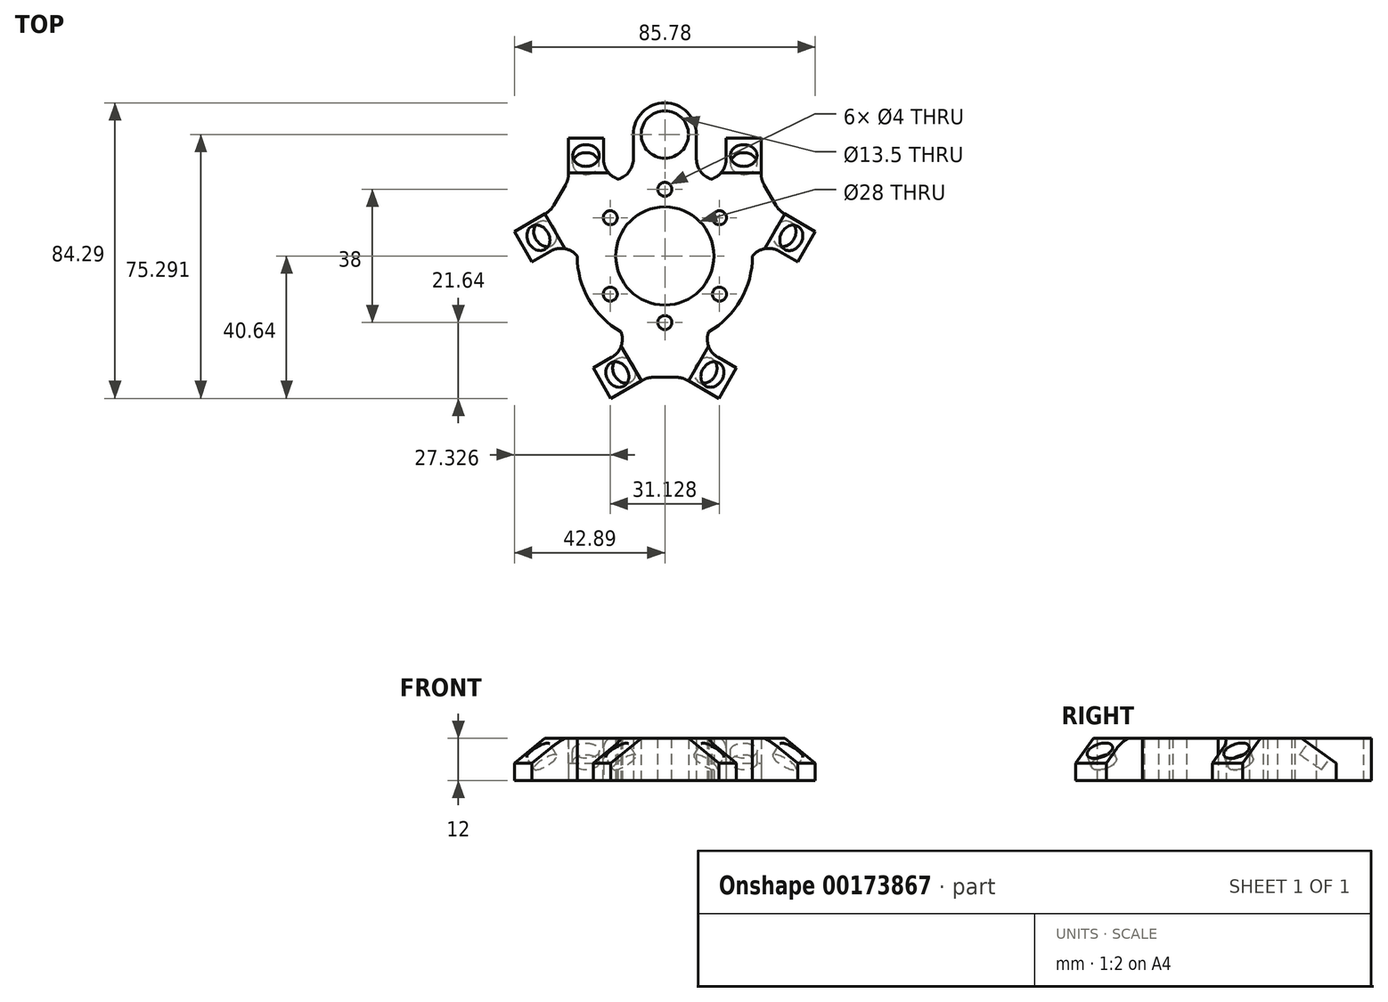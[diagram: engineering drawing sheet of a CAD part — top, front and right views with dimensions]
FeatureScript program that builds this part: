
annotation { "Feature Type Name" : "Feature", "Feature Type Description" : "" }
export const myFeature = defineFeature(function(context is Context, id is Id, definition is map)
    precondition{}
    {
        {
            var Q0;
            Q0=qCreatedBy(makeId("Top.planeOp"),FACE);
            var sketch = newSketch(context, id + "F0", { "sketchPlane" : qUnion([Q0])});
            skCircle(sketch, "E0.cCircle", {"center": v(0, 0) * mm, "radius": 21.65 * mm, "construction": true});
            skLineSegment(sketch, "E0.0", {"start": v(-37.5, 21.65) * mm, "end": v(37.5, 21.65) * mm});
            skLineSegment(sketch, "E0.1", {"start": v(37.5, 21.65) * mm, "end": v(0, -43.3) * mm});
            skLineSegment(sketch, "E0.2", {"start": v(0, -43.3) * mm, "end": v(-37.5, 21.65) * mm});
            skPoint(sketch, "E0.0.midPoint", {"position": v(0, 21.65) * mm});
            skLineSegment(sketch, "E1", {"start": v(-5, -34.64) * mm, "end": v(5, -34.64) * mm});
            skLineSegment(sketch, "E2", {"start": v(27.5, 21.65) * mm, "end": v(32.5, 13) * mm});
            skLineSegment(sketch, "E3", {"start": v(-17.5, 33.65) * mm, "end": v(-17.5, 21.65) * mm});
            skLineSegment(sketch, "E4", {"start": v(17.5, 21.65) * mm, "end": v(17.5, 33.65) * mm});
            skLineSegment(sketch, "E5", {"start": v(27.5, 33.65) * mm, "end": v(27.5, 21.65) * mm});
            skLineSegment(sketch, "E6", {"start": v(-27.5, 21.65) * mm, "end": v(-27.5, 33.65) * mm});
            skLineSegment(sketch, "E7.MirrorCS", {"start": v(32.5, 13) * mm, "end": v(42.9, 7) * mm});
            skLineSegment(sketch, "E8.MirrorCS", {"start": v(37.9, -1.67) * mm, "end": v(27.5, 4.33) * mm});
            skLineSegment(sketch, "E9.MirrorCS", {"start": v(10, -25.98) * mm, "end": v(20.4, -31.98) * mm});
            skLineSegment(sketch, "E10.MirrorCS", {"start": v(15.4, -40.64) * mm, "end": v(5, -34.64) * mm});
            skLineSegment(sketch, "E11", {"start": v(-42.9, 7) * mm, "end": v(-32.5, 13) * mm});
            skLineSegment(sketch, "E12", {"start": v(-37.9, -1.67) * mm, "end": v(-27.5, 4.33) * mm});
            skLineSegment(sketch, "E13", {"start": v(-20.4, -31.98) * mm, "end": v(-10, -25.98) * mm});
            skLineSegment(sketch, "E14", {"start": v(-15.4, -40.64) * mm, "end": v(-5, -34.64) * mm});
            skCircle(sketch, "E15", {"center": v(0, 0) * mm, "radius": 14 * mm});
            skLineSegment(sketch, "E16", {"start": v(0, 21.65) * mm, "end": v(0, 34.65) * mm});
            skCircle(sketch, "E17", {"center": v(0, 34.65) * mm, "radius": 6.75 * mm});
            skArc(sketch, "E18", {"start": v(9, 34.65) * mm, "mid": v(0, 43.65) * mm, "end": v(-9, 34.65) * mm});
            skLineSegment(sketch, "E19", {"start": v(-9, 34.65) * mm, "end": v(-9, 21.65) * mm});
            skLineSegment(sketch, "E20", {"start": v(9, 34.65) * mm, "end": v(9, 21.65) * mm});
            skLineSegment(sketch, "E21", {"start": v(-32.5, 13) * mm, "end": v(-27.5, 21.65) * mm});
            skArc(sketch, "E22", {"start": v(-25, 0) * mm, "mid": v(-21.65, -12.5) * mm, "end": v(-12.5, -21.65) * mm});
            skArc(sketch, "E23.trimOffspring", {"start": v(12.5, -21.65) * mm, "mid": v(21.65, -12.5) * mm, "end": v(25, 0) * mm});
            skLineSegment(sketch, "E24", {"start": v(-37.9, -1.67) * mm, "end": v(-42.9, 7) * mm});
            skLineSegment(sketch, "E25", {"start": v(-27.5, 33.65) * mm, "end": v(-17.5, 33.65) * mm});
            skLineSegment(sketch, "E26", {"start": v(17.5, 33.65) * mm, "end": v(27.5, 33.65) * mm});
            skLineSegment(sketch, "E27", {"start": v(42.9, 7) * mm, "end": v(37.9, -1.67) * mm});
            skLineSegment(sketch, "E28", {"start": v(20.4, -31.98) * mm, "end": v(15.4, -40.64) * mm});
            skLineSegment(sketch, "E29", {"start": v(-15.4, -40.64) * mm, "end": v(-20.4, -31.98) * mm});
            skSolve(sketch);
        }
        {
            var Q0;
            {var subQ0=sQuery(id+"F0.wireOp",EDGE,"E3");Q0=makeQuery(id+"F0.imprint","IMPRINT",FACE,{"disambiguationData":[TD([[makeQuery(id+"F0.imprint","IMPRINT",EDGE,{"derivedFrom":subQ0}),-1.0]])]});}
            var Q1;
            Q1=makeQuery(id+"F0.imprint","IMPRINT",FACE,{"disambiguationData":[TD([[makeQuery(id+"F0.imprint","IMPRINT",EDGE,{"derivedFrom":sQuery(id+"F0.wireOp",EDGE,"E17")}),-1.0]])]});
            var Q2;
            {var subQ2=sQuery(id+"F0.wireOp",EDGE,"E4");Q2=makeQuery(id+"F0.imprint","IMPRINT",FACE,{"disambiguationData":[TD([[makeQuery(id+"F0.imprint","IMPRINT",EDGE,{"derivedFrom":subQ2}),-1.0]])]});}
            var Q3;
            {var subQ19=sQuery(id+"F0.wireOp",EDGE,"E1");Q3=makeQuery(id+"F0.imprint","IMPRINT",FACE,{"disambiguationData":[TD([[makeQuery(id+"F0.imprint","IMPRINT",EDGE,{"derivedFrom":subQ19}),1.0]])]});}
            var Q4;
            {var subQ0=sQuery(id+"F0.wireOp",EDGE,"E7.MirrorCS");Q4=makeQuery(id+"F0.imprint","IMPRINT",FACE,{"disambiguationData":[TD([[makeQuery(id+"F0.imprint","IMPRINT",EDGE,{"derivedFrom":subQ0}),-1.0]])]});}
            var Q5;
            {var subQ2=sQuery(id+"F0.wireOp",EDGE,"E9.MirrorCS");Q5=makeQuery(id+"F0.imprint","IMPRINT",FACE,{"disambiguationData":[TD([[makeQuery(id+"F0.imprint","IMPRINT",EDGE,{"derivedFrom":subQ2}),-1.0]])]});}
            var Q6;
            {var subQ0=sQuery(id+"F0.wireOp",EDGE,"E11");Q6=makeQuery(id+"F0.imprint","IMPRINT",FACE,{"disambiguationData":[TD([[makeQuery(id+"F0.imprint","IMPRINT",EDGE,{"derivedFrom":subQ0}),-1.0]])]});}
            var Q7;
            {var subQ0=sQuery(id+"F0.wireOp",EDGE,"E22");Q7=makeQuery(id+"F0.imprint","IMPRINT",FACE,{"disambiguationData":[TD([[makeQuery(id+"F0.imprint","IMPRINT",EDGE,{"derivedFrom":subQ0}),1.0]])]});}
            var Q8;
            {var subQ0=sQuery(id+"F0.wireOp",EDGE,"E23.trimOffspring");Q8=makeQuery(id+"F0.imprint","IMPRINT",FACE,{"disambiguationData":[TD([[makeQuery(id+"F0.imprint","IMPRINT",EDGE,{"derivedFrom":subQ0}),1.0]])]});}
            var Q9;
            {var subQ2=sQuery(id+"F0.wireOp",EDGE,"E13");Q9=makeQuery(id+"F0.imprint","IMPRINT",FACE,{"disambiguationData":[TD([[makeQuery(id+"F0.imprint","IMPRINT",EDGE,{"derivedFrom":subQ2}),-1.0]])]});}
            extrude(context, id + "F1", {"entities" : qUnion([Q0, Q1, Q2, Q3, Q4, Q5, Q6, Q7, Q8, Q9]), "depth" : 12 * mm});
        }
        {
            var Q0;
            Q0=makeQuery(id+"F1.opExtrude","CAP_EDGE",EDGE,{"disambiguationData":[OSD([sQuery(id+"F0.wireOp",EDGE,"E29")])],"isStart":false});
            var Q1;
            Q1=makeQuery(id+"F1.opExtrude","CAP_EDGE",EDGE,{"disambiguationData":[OSD([sQuery(id+"F0.wireOp",EDGE,"E24")])],"isStart":false});
            var Q2;
            Q2=makeQuery(id+"F1.opExtrude","CAP_EDGE",EDGE,{"disambiguationData":[OSD([sQuery(id+"F0.wireOp",EDGE,"E25")])],"isStart":false});
            var Q3;
            Q3=makeQuery(id+"F1.opExtrude","CAP_EDGE",EDGE,{"disambiguationData":[OSD([sQuery(id+"F0.wireOp",EDGE,"E26")])],"isStart":false});
            var Q4;
            Q4=makeQuery(id+"F1.opExtrude","CAP_EDGE",EDGE,{"disambiguationData":[OSD([sQuery(id+"F0.wireOp",EDGE,"E27")])],"isStart":false});
            var Q5;
            Q5=makeQuery(id+"F1.opExtrude","CAP_EDGE",EDGE,{"disambiguationData":[OSD([sQuery(id+"F0.wireOp",EDGE,"E28")])],"isStart":false});
            chamfer(context, id + "F2", {"entities" : qUnion([Q0, Q1, Q2, Q3, Q4, Q5]), "chamferType" : ChamferType.TWO_OFFSETS, "width1" : 7 * mm, "oppositeDirection" : false, "width2" : 10 * mm, "tangentPropagation" : true});
        }
        {
            var Q0;
            Q0=makeQuery(id+"F2.opChamfer","BLEND_FACE",FACE,{"disambiguationData":[OSD([sQuery(id+"F0.wireOp",EDGE,"E24")])]});
            var sketch = newSketch(context, id + "F3", { "sketchPlane" : qUnion([Q0])});
            skLineSegment(sketch, "E30", {"start": v(-31.04, 11.77) * mm, "end": v(-27.27, 6.41) * mm, "construction": true});
            skLineSegment(sketch, "E31", {"start": v(-33.15, 4.16) * mm, "end": v(-26.05, 9.16) * mm, "construction": true});
            skCircle(sketch, "E32", {"center": v(-28.16, 7.68) * mm, "radius": 3.8 * mm});
            skCircle(sketch, "E33", {"center": v(-2.24, -29.1) * mm, "radius": 3.8 * mm});
            skLineSegment(sketch, "E34", {"start": v(-28.16, 7.68) * mm, "end": v(-2.24, -29.1) * mm, "construction": true});
            skSolve(sketch);
        }
        {
            var Q0;
            Q0=makeQuery(id+"F3.imprint","IMPRINT",FACE,{"disambiguationData":[TD([[makeQuery(id+"F3.imprint","IMPRINT",EDGE,{"derivedFrom":sQuery(id+"F3.wireOp",EDGE,"E32")}),1.0]])]});
            var Q1;
            Q1=makeQuery(id+"F3.imprint","IMPRINT",FACE,{"disambiguationData":[TD([[makeQuery(id+"F3.imprint","IMPRINT",EDGE,{"derivedFrom":sQuery(id+"F3.wireOp",EDGE,"E33")}),1.0]])]});
            extrude(context, id + "F4", {"entities" : qUnion([Q0, Q1]), "operationType" : NewBodyOperationType.REMOVE, "oppositeDirection" : true, "depth" : 4 * mm});
        }
        {
            var Q0;
            Q0=makeQuery(id+"F2.opChamfer","BLEND_FACE",FACE,{"disambiguationData":[OSD([sQuery(id+"F0.wireOp",EDGE,"E26")])]});
            var sketch = newSketch(context, id + "F5", { "sketchPlane" : qUnion([Q0])});
            skLineSegment(sketch, "E35", {"start": v(27.5, 18.6) * mm, "end": v(22.5, 18.6) * mm});
            skLineSegment(sketch, "E36", {"start": v(22.5, 18.6) * mm, "end": v(-22.5, 18.6) * mm});
            skCircle(sketch, "E37", {"center": v(22.5, 18.6) * mm, "radius": 3.8 * mm});
            skCircle(sketch, "E38", {"center": v(-22.5, 18.6) * mm, "radius": 3.8 * mm});
            skSolve(sketch);
        }
        {
            var Q0;
            {var subQ0=sQuery(id+"F5.wireOp",EDGE,"E36");var subQ1=sQuery(id+"F5.wireOp",EDGE,"E35");var subQ2=makeQuery(id+"F5.imprint","INTERSECT",VERTEX,{"derivedFrom":[subQ1,subQ0]});Q0=makeQuery(id+"F5.imprint","IMPRINT",FACE,{"disambiguationData":[TD([[makeQuery(id+"F5.imprint","IMPRINT",EDGE,{"disambiguationData":[TD([[subQ2,1.0]])],"derivedFrom":subQ1}),1.0]])]});}
            var Q1;
            {var subQ0=sQuery(id+"F5.wireOp",EDGE,"E36");var subQ1=sQuery(id+"F5.wireOp",EDGE,"E35");var subQ2=makeQuery(id+"F5.imprint","INTERSECT",VERTEX,{"derivedFrom":[subQ1,subQ0]});Q1=makeQuery(id+"F5.imprint","IMPRINT",FACE,{"disambiguationData":[TD([[makeQuery(id+"F5.imprint","IMPRINT",EDGE,{"disambiguationData":[TD([[subQ2,1.0]])],"derivedFrom":subQ1}),-1.0]])]});}
            var Q2;
            Q2=makeQuery(id+"F5.imprint","IMPRINT",FACE,{"disambiguationData":[TD([[makeQuery(id+"F5.imprint","IMPRINT",EDGE,{"derivedFrom":sQuery(id+"F5.wireOp",EDGE,"E38")}),1.0]])]});
            extrude(context, id + "F6", {"entities" : qUnion([Q0, Q1, Q2]), "operationType" : NewBodyOperationType.REMOVE, "oppositeDirection" : true, "depth" : 4 * mm});
        }
        {
            var Q0;
            Q0=makeQuery(id+"F2.opChamfer","BLEND_FACE",FACE,{"disambiguationData":[OSD([sQuery(id+"F0.wireOp",EDGE,"E28")])]});
            var sketch = newSketch(context, id + "F7", { "sketchPlane" : qUnion([Q0])});
            skLineSegment(sketch, "E39", {"start": v(-0.64, -33.2) * mm, "end": v(2.24, -29.1) * mm});
            skLineSegment(sketch, "E40", {"start": v(2.24, -29.1) * mm, "end": v(28.16, 7.68) * mm});
            skCircle(sketch, "E41", {"center": v(2.24, -29.1) * mm, "radius": 3.8 * mm});
            skCircle(sketch, "E42", {"center": v(28.16, 7.68) * mm, "radius": 3.8 * mm});
            skSolve(sketch);
        }
        {
            var Q0;
            {var subQ0=sQuery(id+"F7.wireOp",EDGE,"E40");var subQ1=sQuery(id+"F7.wireOp",EDGE,"E39");var subQ2=makeQuery(id+"F7.imprint","INTERSECT",VERTEX,{"derivedFrom":[subQ1,subQ0]});Q0=makeQuery(id+"F7.imprint","IMPRINT",FACE,{"disambiguationData":[TD([[makeQuery(id+"F7.imprint","IMPRINT",EDGE,{"disambiguationData":[TD([[subQ2,1.0]])],"derivedFrom":subQ1}),-1.0]])]});}
            var Q1;
            {var subQ0=sQuery(id+"F7.wireOp",EDGE,"E40");var subQ1=sQuery(id+"F7.wireOp",EDGE,"E39");var subQ2=makeQuery(id+"F7.imprint","INTERSECT",VERTEX,{"derivedFrom":[subQ1,subQ0]});Q1=makeQuery(id+"F7.imprint","IMPRINT",FACE,{"disambiguationData":[TD([[makeQuery(id+"F7.imprint","IMPRINT",EDGE,{"disambiguationData":[TD([[subQ2,1.0]])],"derivedFrom":subQ1}),1.0]])]});}
            var Q2;
            Q2=makeQuery(id+"F7.imprint","IMPRINT",FACE,{"disambiguationData":[TD([[makeQuery(id+"F7.imprint","IMPRINT",EDGE,{"derivedFrom":sQuery(id+"F7.wireOp",EDGE,"E42")}),1.0]])]});
            extrude(context, id + "F8", {"entities" : qUnion([Q0, Q1, Q2]), "operationType" : NewBodyOperationType.REMOVE, "oppositeDirection" : true, "depth" : 4 * mm});
        }
        {
            var Q0;
            Q0=makeQuery(id+"F1.opExtrude","CAP_FACE",FACE,{"disambiguationData":[OSD([sQuery(id+"F0.wireOp",EDGE,"E0.0"),sQuery(id+"F0.wireOp",EDGE,"E0.1"),sQuery(id+"F0.wireOp",EDGE,"E0.2"),sQuery(id+"F0.wireOp",EDGE,"E1"),sQuery(id+"F0.wireOp",EDGE,"E2"),sQuery(id+"F0.wireOp",EDGE,"4yodVnod-HSkP-hWuY-k5Q9-o2vyupEBQnbU"),sQuery(id+"F0.wireOp",EDGE,"E3"),sQuery(id+"F0.wireOp",EDGE,"DrTCFwwd-uJIO-l7Mc-FUeM-3Znudd7SfULi"),sQuery(id+"F0.wireOp",EDGE,"XJd8ivhQ-aFTZ-Wpu1-i3gc-w7BEuMXScrIg"),sQuery(id+"F0.wireOp",EDGE,"NkbWxuBs-xui2-Ugcs-E7hZ-WqPHm2JgyJjQ"),sQuery(id+"F0.wireOp",EDGE,"wxoEi51N-vPjQ-D9ZL-bqxc-PpyKxLyGMqhi"),sQuery(id+"F0.wireOp",EDGE,"FRBufPZZ-bnoo-GLsI-h1R0-5fheKrHQj5qL"),sQuery(id+"F0.wireOp",EDGE,"weCBSG1R-y6NJ-jWrY-gTpv-LjhZX11R3FDU"),sQuery(id+"F0.wireOp",EDGE,"E4"),sQuery(id+"F0.wireOp",EDGE,"RQwynOZ9-mmGK-Vg8d-z1nS-SzItJ1ZbRz1E"),sQuery(id+"F0.wireOp",EDGE,"E5"),sQuery(id+"F0.wireOp",EDGE,"E6"),sQuery(id+"F0.wireOp",EDGE,"1b8d74d8-3f0b-407f-a6e8-cb5342e333a70.MirrorCS"),sQuery(id+"F0.wireOp",EDGE,"af4517e1-7c06-4913-bf30-ce8e1029422a0.MirrorCS"),sQuery(id+"F0.wireOp",EDGE,"E7.MirrorCS"),sQuery(id+"F0.wireOp",EDGE,"af4517e1-7c06-4913-bf30-ce8e1029422a2.MirrorCS"),sQuery(id+"F0.wireOp",EDGE,"af4517e1-7c06-4913-bf30-ce8e1029422a3.MirrorCS"),sQuery(id+"F0.wireOp",EDGE,"E8.MirrorCS"),sQuery(id+"F0.wireOp",EDGE,"af4517e1-7c06-4913-bf30-ce8e1029422a5.MirrorCS"),sQuery(id+"F0.wireOp",EDGE,"af4517e1-7c06-4913-bf30-ce8e1029422a6.MirrorCS"),sQuery(id+"F0.wireOp",EDGE,"af4517e1-7c06-4913-bf30-ce8e1029422a7.MirrorCS"),sQuery(id+"F0.wireOp",EDGE,"E9.MirrorCS"),sQuery(id+"F0.wireOp",EDGE,"af4517e1-7c06-4913-bf30-ce8e1029422a9.MirrorCS"),sQuery(id+"F0.wireOp",EDGE,"E70.MirrorCS"),sQuery(id+"F0.wireOp",EDGE,"E10.MirrorCS"),sQuery(id+"F0.wireOp",EDGE,"E11"),sQuery(id+"F0.wireOp",EDGE,"E12"),sQuery(id+"F0.wireOp",EDGE,"918e0306-1a75-4efb-b666-a2afadbdaebc.MirrorCS"),sQuery(id+"F0.wireOp",EDGE,"8d927deb-9123-4b07-8d17-edf002e506ed"),sQuery(id+"F0.wireOp",EDGE,"8b6f3380-b972-40d3-8b0b-d0e01004c041"),sQuery(id+"F0.wireOp",EDGE,"f2d8aa4d-a053-4d04-b9da-e15e9ac5b317.MirrorCS"),sQuery(id+"F0.wireOp",EDGE,"055ed72d-0a9a-4cf6-aa84-763c8b792dbf"),sQuery(id+"F0.wireOp",EDGE,"2b70aff8-f68a-4378-b54f-3f54c54aa466"),sQuery(id+"F0.wireOp",EDGE,"1f120e8b-898b-4de3-9566-7b0c2c69de78.MirrorCS"),sQuery(id+"F0.wireOp",EDGE,"E13"),sQuery(id+"F0.wireOp",EDGE,"E14"),sQuery(id+"F0.wireOp",EDGE,"E15"),sQuery(id+"F0.wireOp",EDGE,"E17"),sQuery(id+"F0.wireOp",EDGE,"E18"),sQuery(id+"F0.wireOp",EDGE,"E19"),sQuery(id+"F0.wireOp",EDGE,"E20"),sQuery(id+"F0.wireOp",EDGE,"E21")])],"isStart":false});
            var sketch = newSketch(context, id + "F9", { "sketchPlane" : qUnion([Q0])});
            skLineSegment(sketch, "E43", {"start": v(0, 0) * mm, "end": v(0, -19) * mm, "construction": true});
            skLineSegment(sketch, "E44", {"start": v(0, 0) * mm, "end": v(0, 19) * mm, "construction": true});
            skLineSegment(sketch, "E45", {"start": v(0, 0) * mm, "end": v(-15.56, 10.9) * mm, "construction": true});
            skLineSegment(sketch, "E46", {"start": v(0, 0) * mm, "end": v(15.56, 10.9) * mm, "construction": true});
            skLineSegment(sketch, "E47", {"start": v(0, 0) * mm, "end": v(-15.56, -10.9) * mm, "construction": true});
            skLineSegment(sketch, "E48", {"start": v(0, 0) * mm, "end": v(15.56, -10.9) * mm, "construction": true});
            skCircle(sketch, "E49", {"center": v(-15.56, 10.9) * mm, "radius": 2 * mm});
            skCircle(sketch, "E50", {"center": v(0, 19) * mm, "radius": 2 * mm});
            skCircle(sketch, "E51", {"center": v(-15.56, -10.9) * mm, "radius": 2 * mm});
            skCircle(sketch, "E52", {"center": v(0, -19) * mm, "radius": 2 * mm});
            skCircle(sketch, "E53", {"center": v(15.56, -10.9) * mm, "radius": 2 * mm});
            skCircle(sketch, "E54", {"center": v(15.56, 10.9) * mm, "radius": 2 * mm});
            skSolve(sketch);
        }
        {
            var Q0;
            Q0=qSketchRegion(id+"F9",true);
            extrude(context, id + "F10", {"entities" : qUnion([Q0]), "operationType" : NewBodyOperationType.REMOVE, "oppositeDirection" : true, "depth" : 25 * mm});
        }
        {
            var Q0;
            Q0=makeQuery(id+"F1.opExtrude","SWEPT_EDGE",EDGE,{"disambiguationData":[OSD([sQuery(id+"F0.wireOp",EDGE,"E0.1"),sQuery(id+"F0.wireOp",EDGE,"E9.MirrorCS")])]});
            var Q1;
            Q1=makeQuery(id+"F1.opExtrude","SWEPT_EDGE",EDGE,{"disambiguationData":[OSD([sQuery(id+"F0.wireOp",EDGE,"E0.1"),sQuery(id+"F0.wireOp",EDGE,"E8.MirrorCS")])]});
            var Q2;
            Q2=makeQuery(id+"F1.opExtrude","SWEPT_EDGE",EDGE,{"disambiguationData":[OSD([sQuery(id+"F0.wireOp",EDGE,"E0.1"),sQuery(id+"F0.wireOp",EDGE,"E1"),sQuery(id+"F0.wireOp",EDGE,"E10.MirrorCS")])]});
            var Q3;
            Q3=makeQuery(id+"F1.opExtrude","SWEPT_EDGE",EDGE,{"disambiguationData":[OSD([sQuery(id+"F0.wireOp",EDGE,"E0.2"),sQuery(id+"F0.wireOp",EDGE,"E1"),sQuery(id+"F0.wireOp",EDGE,"E14")])]});
            var Q4;
            Q4=makeQuery(id+"F1.opExtrude","SWEPT_EDGE",EDGE,{"disambiguationData":[OSD([sQuery(id+"F0.wireOp",EDGE,"E0.2"),sQuery(id+"F0.wireOp",EDGE,"E12")])]});
            var Q5;
            Q5=makeQuery(id+"F1.opExtrude","SWEPT_EDGE",EDGE,{"disambiguationData":[OSD([sQuery(id+"F0.wireOp",EDGE,"E0.0"),sQuery(id+"F0.wireOp",EDGE,"E4")])]});
            var Q6;
            Q6=makeQuery(id+"F1.opExtrude","SWEPT_EDGE",EDGE,{"disambiguationData":[OSD([sQuery(id+"F0.wireOp",EDGE,"E0.2"),sQuery(id+"F0.wireOp",EDGE,"E13")])]});
            var Q7;
            Q7=makeQuery(id+"F1.opExtrude","SWEPT_EDGE",EDGE,{"disambiguationData":[OSD([sQuery(id+"F0.wireOp",EDGE,"E0.0"),sQuery(id+"F0.wireOp",EDGE,"E2"),sQuery(id+"F0.wireOp",EDGE,"E5")])]});
            var Q8;
            Q8=makeQuery(id+"F1.opExtrude","SWEPT_EDGE",EDGE,{"disambiguationData":[OSD([sQuery(id+"F0.wireOp",EDGE,"E0.1"),sQuery(id+"F0.wireOp",EDGE,"E2"),sQuery(id+"F0.wireOp",EDGE,"E7.MirrorCS")])]});
            var Q9;
            Q9=makeQuery(id+"F1.opExtrude","SWEPT_EDGE",EDGE,{"disambiguationData":[OSD([sQuery(id+"F0.wireOp",EDGE,"E0.0"),sQuery(id+"F0.wireOp",EDGE,"E3")])]});
            var Q10;
            Q10=makeQuery(id+"F1.opExtrude","SWEPT_EDGE",EDGE,{"disambiguationData":[OSD([sQuery(id+"F0.wireOp",EDGE,"E0.2"),sQuery(id+"F0.wireOp",EDGE,"E11"),sQuery(id+"F0.wireOp",EDGE,"E21")])]});
            var Q11;
            Q11=makeQuery(id+"F1.opExtrude","SWEPT_EDGE",EDGE,{"disambiguationData":[OSD([sQuery(id+"F0.wireOp",EDGE,"E0.0"),sQuery(id+"F0.wireOp",EDGE,"E6"),sQuery(id+"F0.wireOp",EDGE,"E21")])]});
            var Q12;
            Q12=makeQuery(id+"F1.opExtrude","SWEPT_EDGE",EDGE,{"disambiguationData":[OSD([sQuery(id+"F0.wireOp",EDGE,"E0.0"),sQuery(id+"F0.wireOp",EDGE,"E20")])]});
            var Q13;
            Q13=makeQuery(id+"F1.opExtrude","SWEPT_EDGE",EDGE,{"disambiguationData":[OSD([sQuery(id+"F0.wireOp",EDGE,"E0.0"),sQuery(id+"F0.wireOp",EDGE,"E19")])]});
            fillet(context, id + "F11", {"entities" : qUnion([Q0, Q1, Q2, Q3, Q4, Q5, Q6, Q7, Q8, Q9, Q10, Q11, Q12, Q13]), "radius" : 6 * mm, "tangentPropagation" : true, "allowEdgeOverflow" : false});
        }
    });
